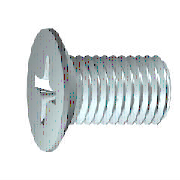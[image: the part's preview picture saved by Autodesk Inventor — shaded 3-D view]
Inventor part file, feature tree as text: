
AUTODESK INVENTOR PART (.ipt)
format: ipt  version: 2022.1 (Build 261234000, 234)  size: 229,376 bytes
history: native  units: mm (DEFAULTED — no unit token found)
features: sketch x1, extrude x1, plane x1
ambient origin geometry x7: Origin, YZ Plane, XZ Plane, X Axis, Y Axis, Z Axis, Center Point
bodies: Solid1 (feature_tree), Body (feature_tree)
feature tree (3):
  sketch  "Sketch1"  dims[d0=25.4mm d1=1.524mm d2=3.5052mm d3=6.0452mm d8=90.0deg d4=2.1844mm d5=3.9116mm d6=4.625123mm d7=10.821041mm d9=19.05mm d10=0.0mm d11=0.472281mm d12=0.472281mm d13=8.726646mm d14=1.524mm d15=25.4mm d45=2.1844mm d16=0.0mm d17=3.9116mm d18=45.0deg d19=1.303867mm d20=1.9558mm d21=3.9116mm d22=0.3429mm d24=0.0mm d25=0.13716mm d62=45.0deg d65=0.0mm d66=0.0mm]
  extrude  "Slot"  Depth=0.13716mm
  plane  "Work Plane2"
